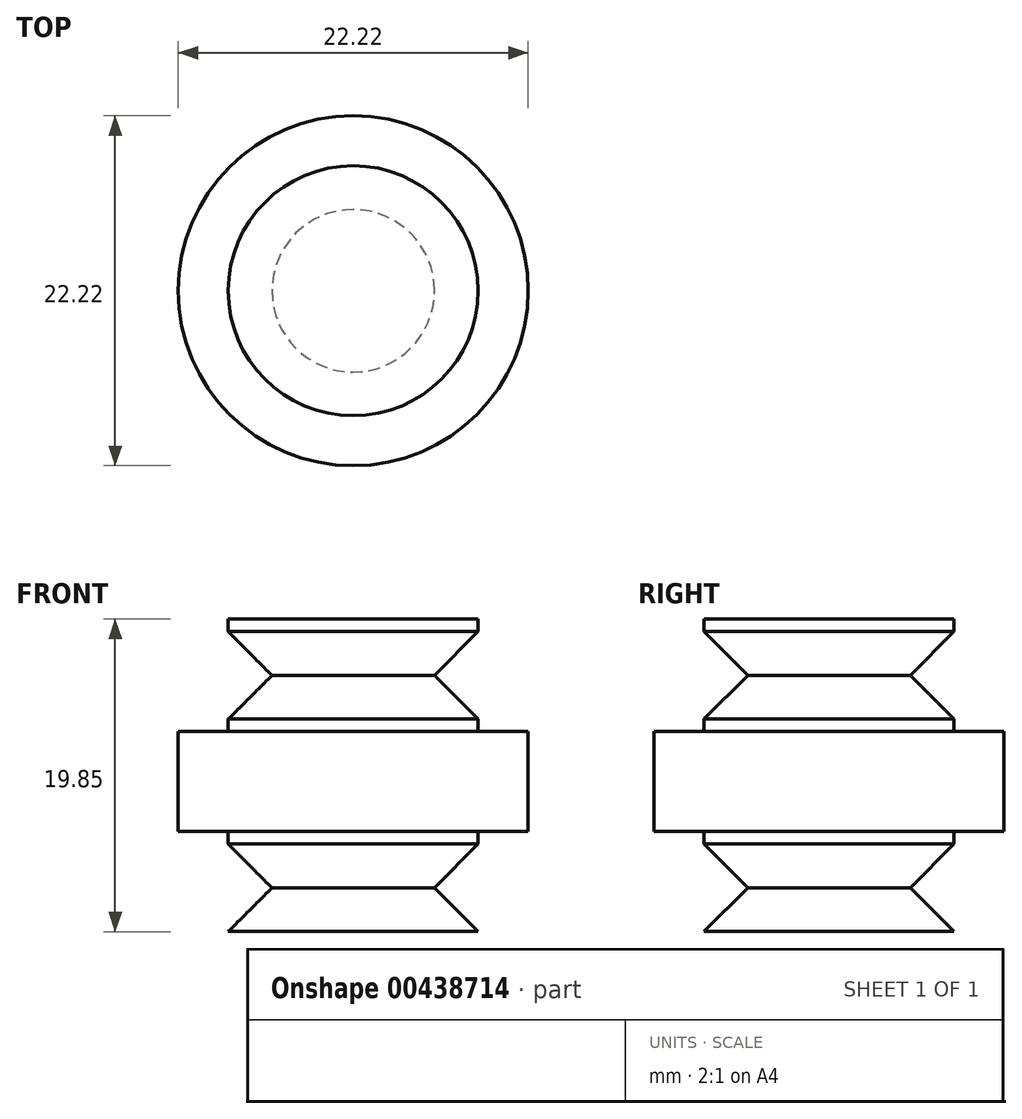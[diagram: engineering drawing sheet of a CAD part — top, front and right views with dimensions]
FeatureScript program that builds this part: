
annotation { "Feature Type Name" : "Feature", "Feature Type Description" : "" }
export const myFeature = defineFeature(function(context is Context, id is Id, definition is map)
    precondition{}
    {
        {
            var Q0;
            Q0=qCreatedBy(makeId("Front.planeOp"),FACE);
            var sketch = newSketch(context, id + "F0", { "sketchPlane" : qUnion([Q0])});
            skLineSegment(sketch, "E0.bottom", {"start": v(-11.11, 3.18) * mm, "end": v(11.11, 3.18) * mm});
            skLineSegment(sketch, "E0.top", {"start": v(-11.11, -3.18) * mm, "end": v(11.11, -3.18) * mm});
            skLineSegment(sketch, "E0.left", {"start": v(-11.11, 3.17) * mm, "end": v(-11.11, -3.18) * mm});
            skLineSegment(sketch, "E0.right", {"start": v(11.11, 3.18) * mm, "end": v(11.11, -3.17) * mm});
            skPoint(sketch, "E0.middle", {"position": v(0, 0) * mm});
            skLineSegment(sketch, "E1.bottom", {"start": v(7.94, 3.18) * mm, "end": v(-7.94, 3.17) * mm});
            skLineSegment(sketch, "E1.top", {"start": v(7.94, 3.97) * mm, "end": v(-7.94, 3.97) * mm});
            skLineSegment(sketch, "E1.left", {"start": v(7.94, 3.17) * mm, "end": v(7.94, 3.97) * mm});
            skLineSegment(sketch, "E1.right", {"start": v(-7.94, 3.17) * mm, "end": v(-7.94, 3.97) * mm});
            skLineSegment(sketch, "E2.bottom", {"start": v(-7.94, -3.18) * mm, "end": v(7.94, -3.18) * mm});
            skLineSegment(sketch, "E2.top", {"start": v(-7.94, -3.97) * mm, "end": v(7.94, -3.97) * mm});
            skLineSegment(sketch, "E2.left", {"start": v(-7.94, -3.18) * mm, "end": v(-7.94, -3.97) * mm});
            skLineSegment(sketch, "E2.right", {"start": v(7.94, -3.18) * mm, "end": v(7.94, -3.97) * mm});
            skLineSegment(sketch, "E3.top", {"start": v(-7.94, 9.52) * mm, "end": v(7.94, 9.52) * mm});
            skLineSegment(sketch, "E4.bottom", {"start": v(-5.16, 3.97) * mm, "end": v(5.16, 3.97) * mm});
            skLineSegment(sketch, "E4.top", {"start": v(-5.16, 6.75) * mm, "end": v(5.16, 6.75) * mm});
            skLineSegment(sketch, "E5", {"start": v(-7.94, 3.97) * mm, "end": v(-5.16, 6.75) * mm});
            skLineSegment(sketch, "E6", {"start": v(-7.94, 9.52) * mm, "end": v(-5.16, 6.75) * mm});
            skLineSegment(sketch, "E7", {"start": v(5.16, 6.75) * mm, "end": v(7.94, 9.52) * mm});
            skLineSegment(sketch, "E8", {"start": v(5.16, 6.75) * mm, "end": v(7.94, 3.97) * mm});
            skLineSegment(sketch, "E9.top", {"start": v(-7.94, 10.32) * mm, "end": v(7.94, 10.32) * mm});
            skLineSegment(sketch, "E9.left", {"start": v(-7.94, 9.52) * mm, "end": v(-7.94, 10.32) * mm});
            skLineSegment(sketch, "E9.right", {"start": v(7.94, 9.52) * mm, "end": v(7.94, 10.32) * mm});
            skLineSegment(sketch, "E10.bottom", {"start": v(7.94, 10.32) * mm, "end": v(7.94, 10.32) * mm});
            skLineSegment(sketch, "E10.top", {"start": v(7.94, 9.52) * mm, "end": v(7.94, 9.52) * mm});
            skLineSegment(sketch, "E10.left", {"start": v(7.94, 10.32) * mm, "end": v(7.94, 9.52) * mm});
            skLineSegment(sketch, "E10.right", {"start": v(7.94, 10.32) * mm, "end": v(7.94, 9.52) * mm});
            skLineSegment(sketch, "E11.bottom", {"start": v(7.94, -3.97) * mm, "end": v(-7.94, -3.97) * mm});
            skLineSegment(sketch, "E11.top", {"start": v(7.94, -9.52) * mm, "end": v(-7.94, -9.53) * mm});
            skLineSegment(sketch, "E12.bottom", {"start": v(5.16, -3.97) * mm, "end": v(-5.16, -3.97) * mm});
            skLineSegment(sketch, "E12.top", {"start": v(5.16, -6.75) * mm, "end": v(-5.16, -6.75) * mm});
            skLineSegment(sketch, "E13", {"start": v(7.94, -3.97) * mm, "end": v(5.16, -6.75) * mm});
            skLineSegment(sketch, "E14", {"start": v(7.94, -9.52) * mm, "end": v(5.16, -6.75) * mm});
            skLineSegment(sketch, "E15", {"start": v(-5.16, -6.75) * mm, "end": v(-7.94, -9.53) * mm});
            skLineSegment(sketch, "E16", {"start": v(-5.16, -6.75) * mm, "end": v(-7.94, -3.97) * mm});
            skLineSegment(sketch, "E17.top", {"start": v(7.94, -10.32) * mm, "end": v(-7.94, -10.32) * mm});
            skLineSegment(sketch, "E17.left", {"start": v(7.94, -9.52) * mm, "end": v(7.94, -10.32) * mm});
            skLineSegment(sketch, "E17.right", {"start": v(-7.94, -9.53) * mm, "end": v(-7.94, -10.32) * mm});
            skLineSegment(sketch, "E18.left", {"start": v(-7.94, -10.32) * mm, "end": v(-7.94, -9.53) * mm});
            skLineSegment(sketch, "E18.right", {"start": v(-7.94, -10.32) * mm, "end": v(-7.94, -9.53) * mm});
            skLineSegment(sketch, "E19", {"start": v(0, -10.32) * mm, "end": v(0, 10.32) * mm});
            skSolve(sketch);
        }
        {
            var Q0;
            {var subQ0=sQuery(id+"F0.wireOp",EDGE,"E6");Q0=makeQuery(id+"F0.imprint","IMPRINT",FACE,{"disambiguationData":[TD([[makeQuery(id+"F0.imprint","IMPRINT",EDGE,{"derivedFrom":subQ0}),1.0]])]});}
            var Q1;
            {var subQ5=sQuery(id+"F0.wireOp",EDGE,"E2.left");Q1=makeQuery(id+"F0.imprint","IMPRINT",FACE,{"disambiguationData":[TD([[makeQuery(id+"F0.imprint","IMPRINT",EDGE,{"derivedFrom":subQ5}),1.0]])]});}
            var Q2;
            {var subQ0=sQuery(id+"F0.wireOp",EDGE,"E15");Q2=makeQuery(id+"F0.imprint","IMPRINT",FACE,{"disambiguationData":[TD([[makeQuery(id+"F0.imprint","IMPRINT",EDGE,{"derivedFrom":subQ0}),1.0]])]});}
            var Q3;
            {var subQ5=sQuery(id+"F0.wireOp",EDGE,"E1.right");Q3=makeQuery(id+"F0.imprint","IMPRINT",FACE,{"disambiguationData":[TD([[makeQuery(id+"F0.imprint","IMPRINT",EDGE,{"derivedFrom":subQ5}),-1.0]])]});}
            var Q4;
            {var subQ0=sQuery(id+"F0.wireOp",EDGE,"E5");Q4=makeQuery(id+"F0.imprint","IMPRINT",FACE,{"disambiguationData":[TD([[makeQuery(id+"F0.imprint","IMPRINT",EDGE,{"derivedFrom":subQ0}),-1.0]])]});}
            var Q5;
            {var subQ0=sQuery(id+"F0.wireOp",EDGE,"E9.left");Q5=makeQuery(id+"F0.imprint","IMPRINT",FACE,{"disambiguationData":[TD([[makeQuery(id+"F0.imprint","IMPRINT",EDGE,{"derivedFrom":subQ0}),-1.0]])]});}
            var Q6;
            {var subQ0=sQuery(id+"F0.wireOp",EDGE,"E0.left");Q6=makeQuery(id+"F0.imprint","IMPRINT",FACE,{"disambiguationData":[TD([[makeQuery(id+"F0.imprint","IMPRINT",EDGE,{"derivedFrom":subQ0}),1.0]])]});}
            var Q7;
            {var subQ0=sQuery(id+"F0.wireOp",EDGE,"E18.right");Q7=makeQuery(id+"F0.imprint","IMPRINT",FACE,{"disambiguationData":[TD([[makeQuery(id+"F0.imprint","IMPRINT",EDGE,{"derivedFrom":subQ0}),-1.0]])]});}
            var Q8;
            {var subQ0=sQuery(id+"F0.wireOp",EDGE,"E16");Q8=makeQuery(id+"F0.imprint","IMPRINT",FACE,{"disambiguationData":[TD([[makeQuery(id+"F0.imprint","IMPRINT",EDGE,{"derivedFrom":subQ0}),-1.0]])]});}
            var Q9;
            Q9=sQuery(id+"F0.wireOp",EDGE,"E19");
            revolve(context, id + "F1", {"entities" : qUnion([Q0, Q1, Q2, Q3, Q4, Q5, Q6, Q7, Q8]), "axis" : qUnion([Q9]), "revolveType" : RevolveType.FULL});
        }
    });
